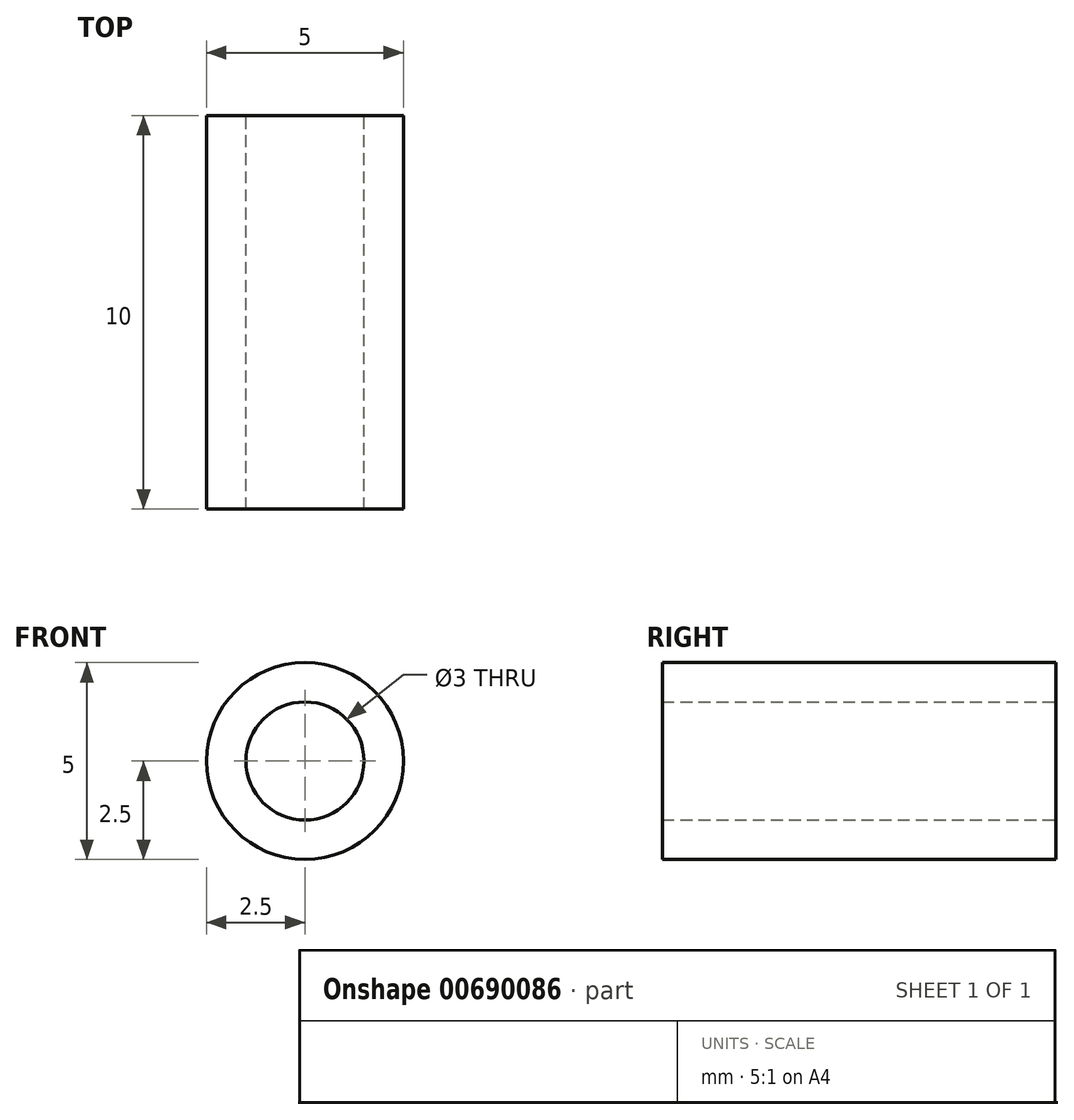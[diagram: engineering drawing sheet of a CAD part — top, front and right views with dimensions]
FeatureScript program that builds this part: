
annotation { "Feature Type Name" : "Feature", "Feature Type Description" : "" }
export const myFeature = defineFeature(function(context is Context, id is Id, definition is map)
    precondition{}
    {
        {
            var Q0;
            Q0=qCreatedBy(makeId("Front.planeOp"),FACE);
            var sketch = newSketch(context, id + "F0", { "sketchPlane" : qUnion([Q0])});
            skCircle(sketch, "E0", {"center": v(0, 0) * mm, "radius": 2.5 * mm});
            skCircle(sketch, "E1", {"center": v(0, 0) * mm, "radius": 1.5 * mm});
            skSolve(sketch);
        }
        {
            var Q0;
            Q0=makeQuery(id+"F0.imprint","IMPRINT",FACE,{"disambiguationData":[TD([[makeQuery(id+"F0.imprint","IMPRINT",EDGE,{"derivedFrom":sQuery(id+"F0.wireOp",EDGE,"E0")}),1.0]])]});
            extrude(context, id + "F1", {"entities" : qUnion([Q0]), "depth" : 10 * mm, "offsetDistance" : 25 * mm});
        }
    });
